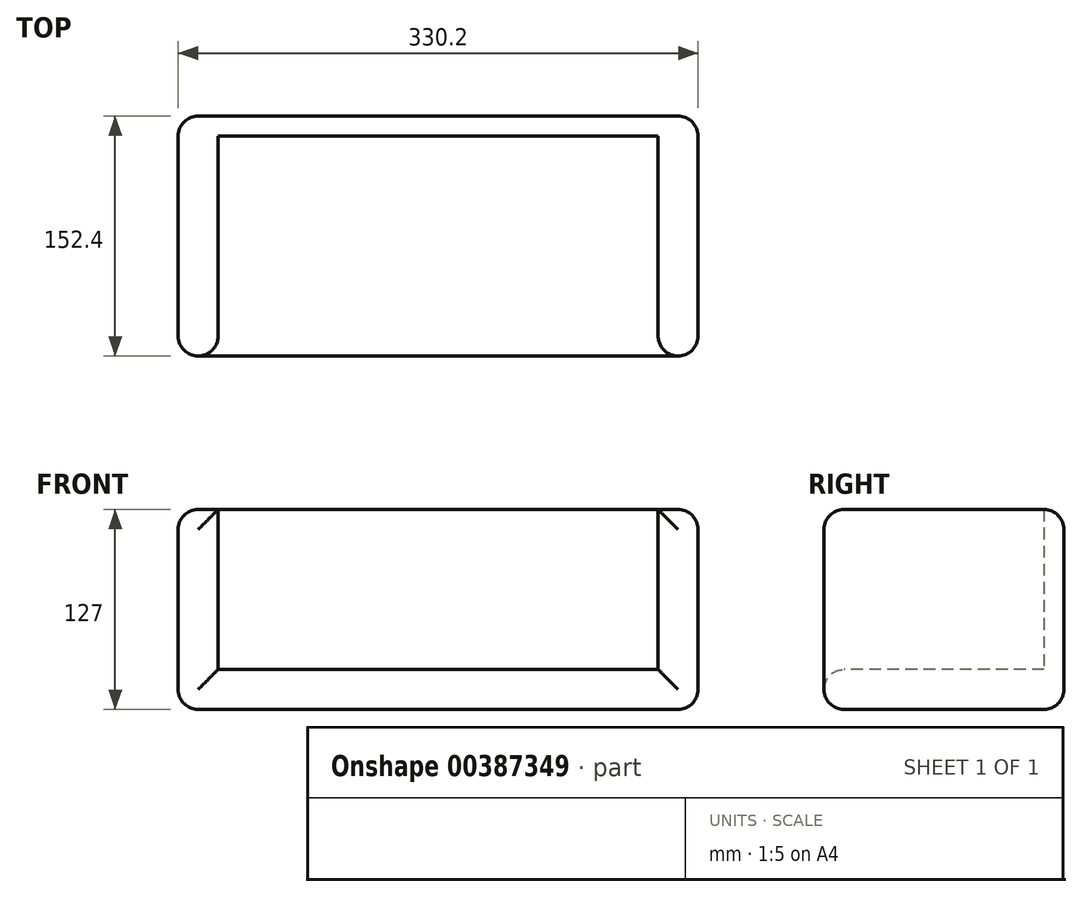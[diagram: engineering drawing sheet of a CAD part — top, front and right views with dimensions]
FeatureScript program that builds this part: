
annotation { "Feature Type Name" : "Feature", "Feature Type Description" : "" }
export const myFeature = defineFeature(function(context is Context, id is Id, definition is map)
    precondition{}
    {
        {
            var Q0;
            Q0=qCreatedBy(makeId("Front.planeOp"),FACE);
            var sketch = newSketch(context, id + "F0", { "sketchPlane" : qUnion([Q0])});
            skLineSegment(sketch, "E0.bottom", {"start": v(-72.3, 34.94) * mm, "end": v(257.9, 34.94) * mm});
            skLineSegment(sketch, "E0.top", {"start": v(-72.3, -92.06) * mm, "end": v(257.9, -92.06) * mm});
            skLineSegment(sketch, "E0.left", {"start": v(-72.3, 34.94) * mm, "end": v(-72.3, -92.06) * mm});
            skLineSegment(sketch, "E0.right", {"start": v(257.9, 34.94) * mm, "end": v(257.9, -92.06) * mm});
            skSolve(sketch);
        }
        {
            var Q0;
            Q0=makeQuery(id+"F0.imprint","IMPRINT",FACE,{"disambiguationData":[TD([[makeQuery(id+"F0.imprint","IMPRINT",EDGE,{"derivedFrom":sQuery(id+"F0.wireOp",EDGE,"E0.bottom")}),-1.0]])]});
            extrude(context, id + "F1", {"entities" : qUnion([Q0]), "depth" : 152.4 * mm});
        }
        {
            var Q0;
            Q0=makeQuery(id+"F1.opExtrude","CAP_FACE",FACE,{"disambiguationData":[OSD([sQuery(id+"F0.wireOp",EDGE,"E0.bottom"),sQuery(id+"F0.wireOp",EDGE,"E0.top"),sQuery(id+"F0.wireOp",EDGE,"E0.left"),sQuery(id+"F0.wireOp",EDGE,"E0.right")])],"isStart":false});
            var sketch = newSketch(context, id + "F2", { "sketchPlane" : qUnion([Q0])});
            skLineSegment(sketch, "E1.bottom", {"start": v(-46.9, 34.94) * mm, "end": v(232.5, 34.94) * mm});
            skLineSegment(sketch, "E1.top", {"start": v(-46.9, -66.66) * mm, "end": v(232.5, -66.66) * mm});
            skLineSegment(sketch, "E1.left", {"start": v(-46.9, 34.94) * mm, "end": v(-46.9, -66.66) * mm});
            skLineSegment(sketch, "E1.right", {"start": v(232.5, 34.94) * mm, "end": v(232.5, -66.66) * mm});
            skLineSegment(sketch, "E2.bottom", {"start": v(101.87, 44.67) * mm, "end": v(157.42, 44.67) * mm});
            skLineSegment(sketch, "E2.top", {"start": v(101.87, 60.96) * mm, "end": v(157.42, 60.96) * mm});
            skLineSegment(sketch, "E2.left", {"start": v(101.87, 44.67) * mm, "end": v(101.87, 60.96) * mm});
            skLineSegment(sketch, "E2.right", {"start": v(157.42, 44.67) * mm, "end": v(157.42, 60.96) * mm});
            skSolve(sketch);
        }
        {
            var Q0;
            Q0=makeQuery(id+"F2.imprint","IMPRINT",FACE,{"disambiguationData":[TD([[makeQuery(id+"F2.imprint","IMPRINT",EDGE,{"derivedFrom":sQuery(id+"F2.wireOp",EDGE,"E1.bottom")}),-1.0]])]});
            extrude(context, id + "F3", {"entities" : qUnion([Q0]), "operationType" : NewBodyOperationType.REMOVE, "oppositeDirection" : true, "depth" : 139.7 * mm});
        }
        {
            var Q0;
            Q0=makeQuery(id+"F1.opExtrude","CAP_EDGE",EDGE,{"disambiguationData":[OSD([sQuery(id+"F0.wireOp",EDGE,"E0.left")])],"isStart":false});
            var Q1;
            Q1=makeQuery(id+"F1.opExtrude","CAP_EDGE",EDGE,{"disambiguationData":[OSD([sQuery(id+"F0.wireOp",EDGE,"E0.right")])],"isStart":false});
            var Q2;
            Q2=makeQuery(id+"F1.opExtrude","SWEPT_FACE",FACE,{"disambiguationData":[OSD([sQuery(id+"F0.wireOp",EDGE,"E0.left")])]});
            var Q3;
            Q3=makeQuery(id+"F1.opExtrude","CAP_FACE",FACE,{"disambiguationData":[OSD([sQuery(id+"F0.wireOp",EDGE,"E0.bottom"),sQuery(id+"F0.wireOp",EDGE,"E0.top"),sQuery(id+"F0.wireOp",EDGE,"E0.left"),sQuery(id+"F0.wireOp",EDGE,"E0.right")])],"isStart":true});
            var Q4;
            Q4=makeQuery(id+"F1.opExtrude","SWEPT_FACE",FACE,{"disambiguationData":[OSD([sQuery(id+"F0.wireOp",EDGE,"E0.right")])]});
            var Q5;
            Q5=makeQuery(id+"F1.opExtrude","CAP_FACE",FACE,{"disambiguationData":[OSD([sQuery(id+"F0.wireOp",EDGE,"E0.bottom"),sQuery(id+"F0.wireOp",EDGE,"E0.top"),sQuery(id+"F0.wireOp",EDGE,"E0.left"),sQuery(id+"F0.wireOp",EDGE,"E0.right")])],"isStart":false});
            fillet(context, id + "F4", {"entities" : qUnion([Q0, Q1, Q2, Q3, Q4, Q5]), "radius" : 12.7 * mm, "tangentPropagation" : true, "allowEdgeOverflow" : false});
        }
    });
